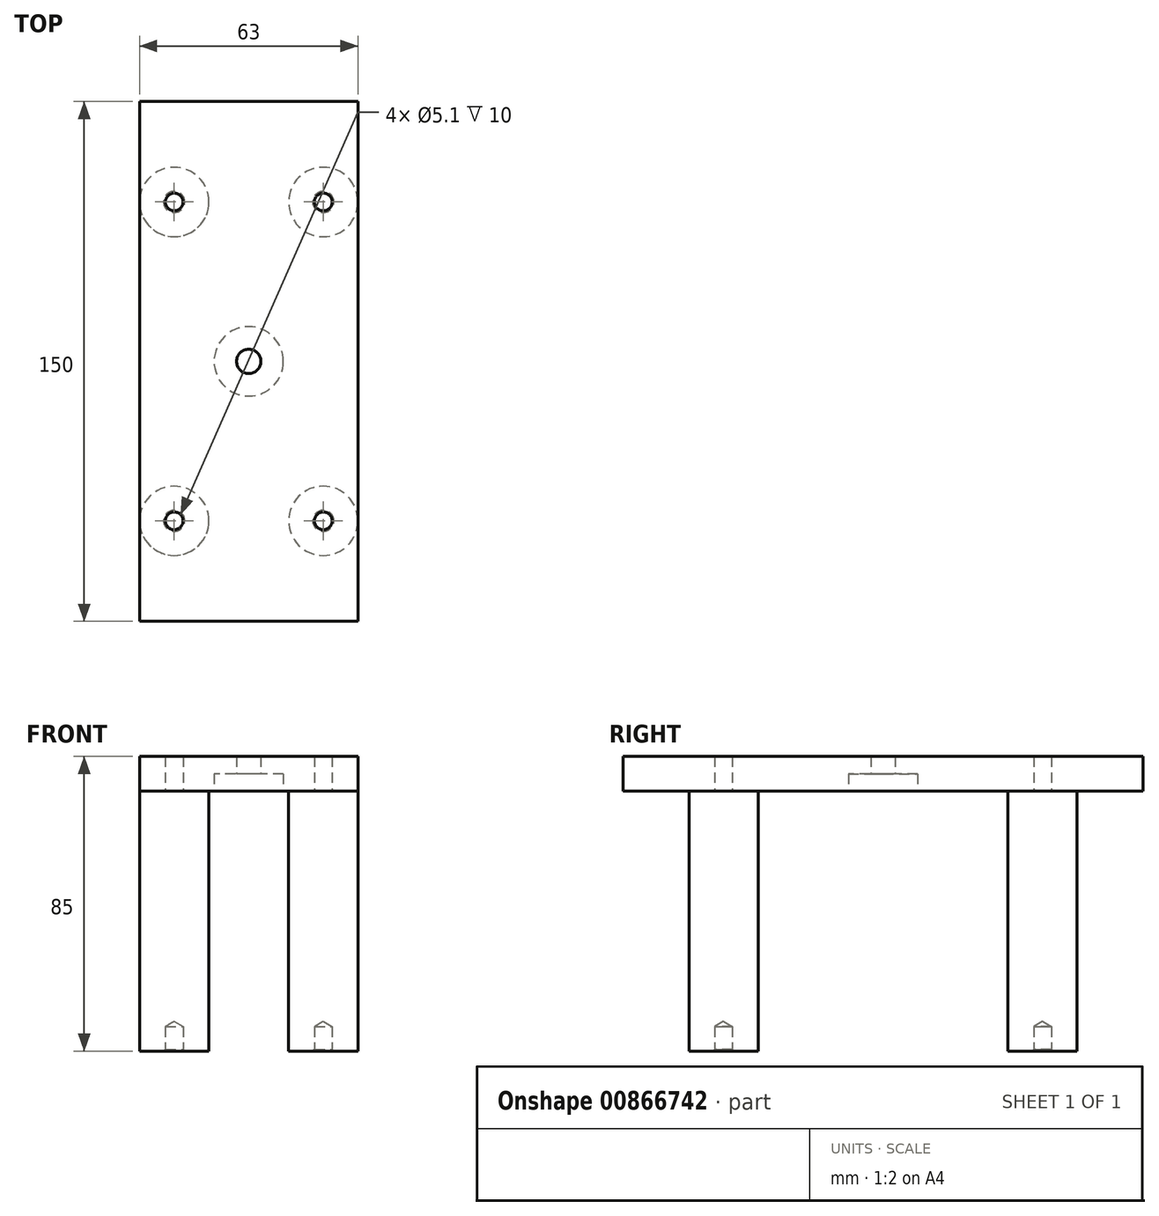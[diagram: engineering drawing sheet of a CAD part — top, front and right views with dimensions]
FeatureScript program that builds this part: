
annotation { "Feature Type Name" : "Feature", "Feature Type Description" : "" }
export const myFeature = defineFeature(function(context is Context, id is Id, definition is map)
    precondition{}
    {
        {
            assignVariable(context, id + "F0", {"variableType" : VariableType.LENGTH, "name" : "PillarLength", "lengthValue" : 75 * mm});
        }
        {
            assignVariable(context, id + "F1", {"variableType" : VariableType.LENGTH, "name" : "RackThickness", "lengthValue" : 10 * mm});
        }
        {
            assignVariable(context, id + "F2", {"variableType" : VariableType.LENGTH, "name" : "InsertWidth", "lengthValue" : 5.1 * mm});
        }
        {
            assignVariable(context, id + "F3", {"variableType" : VariableType.LENGTH, "name" : "InsertDepth", "lengthValue" : 6.4 * mm});
        }
        {
            var Q0;
            Q0=qCreatedBy(makeId("Top.planeOp"),FACE);
            var sketch = newSketch(context, id + "F4", { "sketchPlane" : qUnion([Q0])});
            skLineSegment(sketch, "E0.bottom", {"start": v(31.5, -75) * mm, "end": v(-31.5, -75) * mm});
            skLineSegment(sketch, "E0.top", {"start": v(31.5, 75) * mm, "end": v(-31.5, 75) * mm});
            skLineSegment(sketch, "E0.left", {"start": v(31.5, -75) * mm, "end": v(31.5, 75) * mm});
            skLineSegment(sketch, "E0.right", {"start": v(-31.5, -75) * mm, "end": v(-31.5, 75) * mm});
            skPoint(sketch, "E0.middle", {"position": v(0, 0) * mm});
            skLineSegment(sketch, "E1.bottom", {"start": v(21.5, 46) * mm, "end": v(-21.5, 46) * mm});
            skLineSegment(sketch, "E1.top", {"start": v(21.5, -46) * mm, "end": v(-21.5, -46) * mm});
            skLineSegment(sketch, "E1.left", {"start": v(21.5, 46) * mm, "end": v(21.5, -46) * mm});
            skLineSegment(sketch, "E1.right", {"start": v(-21.5, 46) * mm, "end": v(-21.5, -46) * mm});
            skCircle(sketch, "E2", {"center": v(-21.5, 46) * mm, "radius": 10 * mm});
            skCircle(sketch, "E3", {"center": v(21.5, 46) * mm, "radius": 10 * mm});
            skCircle(sketch, "E4", {"center": v(-21.5, -46) * mm, "radius": 10 * mm});
            skCircle(sketch, "E5", {"center": v(21.5, -46) * mm, "radius": 10 * mm});
            skCircle(sketch, "E6", {"center": v(-21.5, 46) * mm, "radius": 2.55 * mm});
            skCircle(sketch, "E7", {"center": v(21.5, 46) * mm, "radius": 2.55 * mm});
            skCircle(sketch, "E8", {"center": v(-21.5, -46) * mm, "radius": 2.55 * mm});
            skCircle(sketch, "E9", {"center": v(21.5, -46) * mm, "radius": 2.55 * mm});
            skSolve(sketch);
        }
        {
            var Q0;
            {var subQ0=sQuery(id+"F4.wireOp",EDGE,"E5");var subQ1=sQuery(id+"F4.wireOp",EDGE,"E0.left");var subQ2=makeQuery(id+"F4.imprint","INTERSECT",VERTEX,{"derivedFrom":[subQ1,subQ0]});Q0=makeQuery(id+"F4.imprint","IMPRINT",FACE,{"disambiguationData":[TD([[makeQuery(id+"F4.imprint","IMPRINT",EDGE,{"disambiguationData":[TD([[subQ2,-1.0]])],"derivedFrom":subQ1}),1.0]])]});}
            var Q1;
            {var subQ1=sQuery(id+"F4.wireOp",EDGE,"E0.bottom");Q1=makeQuery(id+"F4.imprint","IMPRINT",FACE,{"disambiguationData":[TD([[makeQuery(id+"F4.imprint","IMPRINT",EDGE,{"derivedFrom":subQ1}),-1.0]])]});}
            var Q2;
            {var subQ0=sQuery(id+"F4.wireOp",EDGE,"E4");var subQ1=sQuery(id+"F4.wireOp",EDGE,"E0.right");var subQ2=makeQuery(id+"F4.imprint","INTERSECT",VERTEX,{"derivedFrom":[subQ1,subQ0]});Q2=makeQuery(id+"F4.imprint","IMPRINT",FACE,{"disambiguationData":[TD([[makeQuery(id+"F4.imprint","IMPRINT",EDGE,{"disambiguationData":[TD([[subQ2,-1.0]])],"derivedFrom":subQ1}),-1.0]])]});}
            var Q3;
            {var subQ5=sQuery(id+"F4.wireOp",EDGE,"E3");var subQ13=sQuery(id+"F4.wireOp",EDGE,"E1.bottom");var subQ14=makeQuery(id+"F4.imprint","INTERSECT",VERTEX,{"derivedFrom":[subQ13,subQ5]});Q3=makeQuery(id+"F4.imprint","IMPRINT",FACE,{"disambiguationData":[TD([[makeQuery(id+"F4.imprint","IMPRINT",EDGE,{"disambiguationData":[TD([[subQ14,-1.0]])],"derivedFrom":subQ13}),1.0]])]});}
            var Q4;
            {var subQ0=sQuery(id+"F4.wireOp",EDGE,"E4");var subQ4=sQuery(id+"F4.wireOp",EDGE,"E1.top");var subQ5=makeQuery(id+"F4.imprint","INTERSECT",VERTEX,{"derivedFrom":[subQ4,subQ0]});Q4=makeQuery(id+"F4.imprint","IMPRINT",FACE,{"disambiguationData":[TD([[makeQuery(id+"F4.imprint","IMPRINT",EDGE,{"disambiguationData":[TD([[subQ5,-1.0]])],"derivedFrom":subQ4}),1.0]])]});}
            var Q5;
            {var subQ0=sQuery(id+"F4.wireOp",EDGE,"E4");var subQ1=sQuery(id+"F4.wireOp",EDGE,"E1.top");var subQ2=makeQuery(id+"F4.imprint","INTERSECT",VERTEX,{"derivedFrom":[subQ1,subQ0]});Q5=makeQuery(id+"F4.imprint","IMPRINT",FACE,{"disambiguationData":[TD([[makeQuery(id+"F4.imprint","IMPRINT",EDGE,{"disambiguationData":[TD([[subQ2,-1.0]])],"derivedFrom":subQ1}),-1.0]])]});}
            var Q6;
            {var subQ0=sQuery(id+"F4.wireOp",EDGE,"E1.right");var subQ1=sQuery(id+"F4.wireOp",EDGE,"E1.top");var subQ2=makeQuery(id+"F4.imprint","INTERSECT",VERTEX,{"derivedFrom":[subQ1,subQ0]});Q6=makeQuery(id+"F4.imprint","IMPRINT",FACE,{"disambiguationData":[TD([[makeQuery(id+"F4.imprint","IMPRINT",EDGE,{"disambiguationData":[TD([[subQ2,1.0]])],"derivedFrom":subQ1}),1.0]])]});}
            var Q7;
            {var subQ0=sQuery(id+"F4.wireOp",EDGE,"E1.right");var subQ1=sQuery(id+"F4.wireOp",EDGE,"E1.top");var subQ2=makeQuery(id+"F4.imprint","INTERSECT",VERTEX,{"derivedFrom":[subQ1,subQ0]});Q7=makeQuery(id+"F4.imprint","IMPRINT",FACE,{"disambiguationData":[TD([[makeQuery(id+"F4.imprint","IMPRINT",EDGE,{"disambiguationData":[TD([[subQ2,1.0]])],"derivedFrom":subQ1}),-1.0]])]});}
            var Q8;
            {var subQ4=sQuery(id+"F4.wireOp",EDGE,"E9");var subQ6=sQuery(id+"F4.wireOp",EDGE,"E1.top");var subQ8=makeQuery(id+"F4.imprint","INTERSECT",VERTEX,{"derivedFrom":[subQ6,subQ4]});Q8=makeQuery(id+"F4.imprint","IMPRINT",FACE,{"disambiguationData":[TD([[makeQuery(id+"F4.imprint","IMPRINT",EDGE,{"disambiguationData":[TD([[subQ8,-1.0]])],"derivedFrom":subQ6}),1.0]])]});}
            var Q9;
            {var subQ0=sQuery(id+"F4.wireOp",EDGE,"E1.left");var subQ1=sQuery(id+"F4.wireOp",EDGE,"E1.top");var subQ2=makeQuery(id+"F4.imprint","INTERSECT",VERTEX,{"derivedFrom":[subQ1,subQ0]});Q9=makeQuery(id+"F4.imprint","IMPRINT",FACE,{"disambiguationData":[TD([[makeQuery(id+"F4.imprint","IMPRINT",EDGE,{"disambiguationData":[TD([[subQ2,-1.0]])],"derivedFrom":subQ1}),-1.0]])]});}
            var Q10;
            {var subQ0=sQuery(id+"F4.wireOp",EDGE,"E1.left");var subQ1=sQuery(id+"F4.wireOp",EDGE,"E1.top");var subQ2=makeQuery(id+"F4.imprint","INTERSECT",VERTEX,{"derivedFrom":[subQ1,subQ0]});Q10=makeQuery(id+"F4.imprint","IMPRINT",FACE,{"disambiguationData":[TD([[makeQuery(id+"F4.imprint","IMPRINT",EDGE,{"disambiguationData":[TD([[subQ2,-1.0]])],"derivedFrom":subQ1}),1.0]])]});}
            var Q11;
            {var subQ0=sQuery(id+"F4.wireOp",EDGE,"E9");var subQ1=sQuery(id+"F4.wireOp",EDGE,"E1.top");var subQ2=makeQuery(id+"F4.imprint","INTERSECT",VERTEX,{"derivedFrom":[subQ1,subQ0]});Q11=makeQuery(id+"F4.imprint","IMPRINT",FACE,{"disambiguationData":[TD([[makeQuery(id+"F4.imprint","IMPRINT",EDGE,{"disambiguationData":[TD([[subQ2,-1.0]])],"derivedFrom":subQ1}),-1.0]])]});}
            var Q12;
            {var subQ0=sQuery(id+"F4.wireOp",EDGE,"E7");var subQ1=sQuery(id+"F4.wireOp",EDGE,"E1.bottom");var subQ2=makeQuery(id+"F4.imprint","INTERSECT",VERTEX,{"derivedFrom":[subQ1,subQ0]});Q12=makeQuery(id+"F4.imprint","IMPRINT",FACE,{"disambiguationData":[TD([[makeQuery(id+"F4.imprint","IMPRINT",EDGE,{"disambiguationData":[TD([[subQ2,-1.0]])],"derivedFrom":subQ1}),1.0]])]});}
            var Q13;
            {var subQ0=sQuery(id+"F4.wireOp",EDGE,"E1.left");var subQ1=sQuery(id+"F4.wireOp",EDGE,"E1.bottom");var subQ2=makeQuery(id+"F4.imprint","INTERSECT",VERTEX,{"derivedFrom":[subQ1,subQ0]});Q13=makeQuery(id+"F4.imprint","IMPRINT",FACE,{"disambiguationData":[TD([[makeQuery(id+"F4.imprint","IMPRINT",EDGE,{"disambiguationData":[TD([[subQ2,-1.0]])],"derivedFrom":subQ1}),1.0]])]});}
            var Q14;
            {var subQ0=sQuery(id+"F4.wireOp",EDGE,"E1.left");var subQ1=sQuery(id+"F4.wireOp",EDGE,"E1.bottom");var subQ2=makeQuery(id+"F4.imprint","INTERSECT",VERTEX,{"derivedFrom":[subQ1,subQ0]});Q14=makeQuery(id+"F4.imprint","IMPRINT",FACE,{"disambiguationData":[TD([[makeQuery(id+"F4.imprint","IMPRINT",EDGE,{"disambiguationData":[TD([[subQ2,-1.0]])],"derivedFrom":subQ1}),-1.0]])]});}
            var Q15;
            {var subQ4=sQuery(id+"F4.wireOp",EDGE,"E1.bottom");var subQ6=sQuery(id+"F4.wireOp",EDGE,"E7");var subQ7=makeQuery(id+"F4.imprint","INTERSECT",VERTEX,{"derivedFrom":[subQ4,subQ6]});Q15=makeQuery(id+"F4.imprint","IMPRINT",FACE,{"disambiguationData":[TD([[makeQuery(id+"F4.imprint","IMPRINT",EDGE,{"disambiguationData":[TD([[subQ7,-1.0]])],"derivedFrom":subQ4}),-1.0]])]});}
            var Q16;
            {var subQ0=sQuery(id+"F4.wireOp",EDGE,"E2");var subQ1=sQuery(id+"F4.wireOp",EDGE,"E1.bottom");var subQ2=makeQuery(id+"F4.imprint","INTERSECT",VERTEX,{"derivedFrom":[subQ1,subQ0]});Q16=makeQuery(id+"F4.imprint","IMPRINT",FACE,{"disambiguationData":[TD([[makeQuery(id+"F4.imprint","IMPRINT",EDGE,{"disambiguationData":[TD([[subQ2,-1.0]])],"derivedFrom":subQ1}),1.0]])]});}
            var Q17;
            {var subQ0=sQuery(id+"F4.wireOp",EDGE,"E1.right");var subQ1=sQuery(id+"F4.wireOp",EDGE,"E1.bottom");var subQ2=makeQuery(id+"F4.imprint","INTERSECT",VERTEX,{"derivedFrom":[subQ1,subQ0]});Q17=makeQuery(id+"F4.imprint","IMPRINT",FACE,{"disambiguationData":[TD([[makeQuery(id+"F4.imprint","IMPRINT",EDGE,{"disambiguationData":[TD([[subQ2,1.0]])],"derivedFrom":subQ1}),1.0]])]});}
            var Q18;
            {var subQ0=sQuery(id+"F4.wireOp",EDGE,"E1.right");var subQ1=sQuery(id+"F4.wireOp",EDGE,"E1.bottom");var subQ2=makeQuery(id+"F4.imprint","INTERSECT",VERTEX,{"derivedFrom":[subQ1,subQ0]});Q18=makeQuery(id+"F4.imprint","IMPRINT",FACE,{"disambiguationData":[TD([[makeQuery(id+"F4.imprint","IMPRINT",EDGE,{"disambiguationData":[TD([[subQ2,1.0]])],"derivedFrom":subQ1}),-1.0]])]});}
            var Q19;
            {var subQ0=sQuery(id+"F4.wireOp",EDGE,"E2");var subQ2=sQuery(id+"F4.wireOp",EDGE,"E1.bottom");var subQ3=makeQuery(id+"F4.imprint","INTERSECT",VERTEX,{"derivedFrom":[subQ2,subQ0]});Q19=makeQuery(id+"F4.imprint","IMPRINT",FACE,{"disambiguationData":[TD([[makeQuery(id+"F4.imprint","IMPRINT",EDGE,{"disambiguationData":[TD([[subQ3,-1.0]])],"derivedFrom":subQ2}),-1.0]])]});}
            var Q20;
            {var subQ6=sQuery(id+"F4.wireOp",EDGE,"E0.top");Q20=makeQuery(id+"F4.imprint","IMPRINT",FACE,{"disambiguationData":[TD([[makeQuery(id+"F4.imprint","IMPRINT",EDGE,{"derivedFrom":subQ6}),1.0]])]});}
            extrude(context, id + "F5", {"entities" : qUnion([Q0, Q1, Q2, Q3, Q4, Q5, Q6, Q7, Q8, Q9, Q10, Q11, Q12, Q13, Q14, Q15, Q16, Q17, Q18, Q19, Q20]), "depth" : getVariable(context, 'RackThickness'), "offsetDistance" : 25 * mm});
        }
        {
            var Q0;
            {var subQ0=sQuery(id+"F4.wireOp",EDGE,"E7");var subQ1=sQuery(id+"F4.wireOp",EDGE,"E1.bottom");var subQ2=makeQuery(id+"F4.imprint","INTERSECT",VERTEX,{"derivedFrom":[subQ1,subQ0]});Q0=makeQuery(id+"F4.imprint","IMPRINT",FACE,{"disambiguationData":[TD([[makeQuery(id+"F4.imprint","IMPRINT",EDGE,{"disambiguationData":[TD([[subQ2,-1.0]])],"derivedFrom":subQ1}),1.0]])]});}
            var Q1;
            {var subQ4=sQuery(id+"F4.wireOp",EDGE,"E1.bottom");var subQ6=sQuery(id+"F4.wireOp",EDGE,"E7");var subQ7=makeQuery(id+"F4.imprint","INTERSECT",VERTEX,{"derivedFrom":[subQ4,subQ6]});Q1=makeQuery(id+"F4.imprint","IMPRINT",FACE,{"disambiguationData":[TD([[makeQuery(id+"F4.imprint","IMPRINT",EDGE,{"disambiguationData":[TD([[subQ7,-1.0]])],"derivedFrom":subQ4}),-1.0]])]});}
            var Q2;
            {var subQ0=sQuery(id+"F4.wireOp",EDGE,"E1.left");var subQ1=sQuery(id+"F4.wireOp",EDGE,"E1.bottom");var subQ2=makeQuery(id+"F4.imprint","INTERSECT",VERTEX,{"derivedFrom":[subQ1,subQ0]});Q2=makeQuery(id+"F4.imprint","IMPRINT",FACE,{"disambiguationData":[TD([[makeQuery(id+"F4.imprint","IMPRINT",EDGE,{"disambiguationData":[TD([[subQ2,-1.0]])],"derivedFrom":subQ1}),-1.0]])]});}
            var Q3;
            {var subQ0=sQuery(id+"F4.wireOp",EDGE,"E1.left");var subQ1=sQuery(id+"F4.wireOp",EDGE,"E1.bottom");var subQ2=makeQuery(id+"F4.imprint","INTERSECT",VERTEX,{"derivedFrom":[subQ1,subQ0]});Q3=makeQuery(id+"F4.imprint","IMPRINT",FACE,{"disambiguationData":[TD([[makeQuery(id+"F4.imprint","IMPRINT",EDGE,{"disambiguationData":[TD([[subQ2,-1.0]])],"derivedFrom":subQ1}),1.0]])]});}
            var Q4;
            {var subQ0=sQuery(id+"F4.wireOp",EDGE,"E2");var subQ1=sQuery(id+"F4.wireOp",EDGE,"E1.bottom");var subQ2=makeQuery(id+"F4.imprint","INTERSECT",VERTEX,{"derivedFrom":[subQ1,subQ0]});Q4=makeQuery(id+"F4.imprint","IMPRINT",FACE,{"disambiguationData":[TD([[makeQuery(id+"F4.imprint","IMPRINT",EDGE,{"disambiguationData":[TD([[subQ2,-1.0]])],"derivedFrom":subQ1}),1.0]])]});}
            var Q5;
            {var subQ0=sQuery(id+"F4.wireOp",EDGE,"E2");var subQ2=sQuery(id+"F4.wireOp",EDGE,"E1.bottom");var subQ3=makeQuery(id+"F4.imprint","INTERSECT",VERTEX,{"derivedFrom":[subQ2,subQ0]});Q5=makeQuery(id+"F4.imprint","IMPRINT",FACE,{"disambiguationData":[TD([[makeQuery(id+"F4.imprint","IMPRINT",EDGE,{"disambiguationData":[TD([[subQ3,-1.0]])],"derivedFrom":subQ2}),-1.0]])]});}
            var Q6;
            {var subQ0=sQuery(id+"F4.wireOp",EDGE,"E1.right");var subQ1=sQuery(id+"F4.wireOp",EDGE,"E1.bottom");var subQ2=makeQuery(id+"F4.imprint","INTERSECT",VERTEX,{"derivedFrom":[subQ1,subQ0]});Q6=makeQuery(id+"F4.imprint","IMPRINT",FACE,{"disambiguationData":[TD([[makeQuery(id+"F4.imprint","IMPRINT",EDGE,{"disambiguationData":[TD([[subQ2,1.0]])],"derivedFrom":subQ1}),1.0]])]});}
            var Q7;
            {var subQ0=sQuery(id+"F4.wireOp",EDGE,"E1.right");var subQ1=sQuery(id+"F4.wireOp",EDGE,"E1.bottom");var subQ2=makeQuery(id+"F4.imprint","INTERSECT",VERTEX,{"derivedFrom":[subQ1,subQ0]});Q7=makeQuery(id+"F4.imprint","IMPRINT",FACE,{"disambiguationData":[TD([[makeQuery(id+"F4.imprint","IMPRINT",EDGE,{"disambiguationData":[TD([[subQ2,1.0]])],"derivedFrom":subQ1}),-1.0]])]});}
            var Q8;
            {var subQ0=sQuery(id+"F4.wireOp",EDGE,"E1.right");var subQ1=sQuery(id+"F4.wireOp",EDGE,"E1.top");var subQ2=makeQuery(id+"F4.imprint","INTERSECT",VERTEX,{"derivedFrom":[subQ1,subQ0]});Q8=makeQuery(id+"F4.imprint","IMPRINT",FACE,{"disambiguationData":[TD([[makeQuery(id+"F4.imprint","IMPRINT",EDGE,{"disambiguationData":[TD([[subQ2,1.0]])],"derivedFrom":subQ1}),1.0]])]});}
            var Q9;
            {var subQ0=sQuery(id+"F4.wireOp",EDGE,"E1.right");var subQ1=sQuery(id+"F4.wireOp",EDGE,"E1.top");var subQ2=makeQuery(id+"F4.imprint","INTERSECT",VERTEX,{"derivedFrom":[subQ1,subQ0]});Q9=makeQuery(id+"F4.imprint","IMPRINT",FACE,{"disambiguationData":[TD([[makeQuery(id+"F4.imprint","IMPRINT",EDGE,{"disambiguationData":[TD([[subQ2,1.0]])],"derivedFrom":subQ1}),-1.0]])]});}
            var Q10;
            {var subQ0=sQuery(id+"F4.wireOp",EDGE,"E4");var subQ1=sQuery(id+"F4.wireOp",EDGE,"E1.top");var subQ2=makeQuery(id+"F4.imprint","INTERSECT",VERTEX,{"derivedFrom":[subQ1,subQ0]});Q10=makeQuery(id+"F4.imprint","IMPRINT",FACE,{"disambiguationData":[TD([[makeQuery(id+"F4.imprint","IMPRINT",EDGE,{"disambiguationData":[TD([[subQ2,-1.0]])],"derivedFrom":subQ1}),-1.0]])]});}
            var Q11;
            {var subQ0=sQuery(id+"F4.wireOp",EDGE,"E4");var subQ4=sQuery(id+"F4.wireOp",EDGE,"E1.top");var subQ5=makeQuery(id+"F4.imprint","INTERSECT",VERTEX,{"derivedFrom":[subQ4,subQ0]});Q11=makeQuery(id+"F4.imprint","IMPRINT",FACE,{"disambiguationData":[TD([[makeQuery(id+"F4.imprint","IMPRINT",EDGE,{"disambiguationData":[TD([[subQ5,-1.0]])],"derivedFrom":subQ4}),1.0]])]});}
            var Q12;
            {var subQ0=sQuery(id+"F4.wireOp",EDGE,"E1.left");var subQ1=sQuery(id+"F4.wireOp",EDGE,"E1.top");var subQ2=makeQuery(id+"F4.imprint","INTERSECT",VERTEX,{"derivedFrom":[subQ1,subQ0]});Q12=makeQuery(id+"F4.imprint","IMPRINT",FACE,{"disambiguationData":[TD([[makeQuery(id+"F4.imprint","IMPRINT",EDGE,{"disambiguationData":[TD([[subQ2,-1.0]])],"derivedFrom":subQ1}),1.0]])]});}
            var Q13;
            {var subQ0=sQuery(id+"F4.wireOp",EDGE,"E1.left");var subQ1=sQuery(id+"F4.wireOp",EDGE,"E1.top");var subQ2=makeQuery(id+"F4.imprint","INTERSECT",VERTEX,{"derivedFrom":[subQ1,subQ0]});Q13=makeQuery(id+"F4.imprint","IMPRINT",FACE,{"disambiguationData":[TD([[makeQuery(id+"F4.imprint","IMPRINT",EDGE,{"disambiguationData":[TD([[subQ2,-1.0]])],"derivedFrom":subQ1}),-1.0]])]});}
            var Q14;
            {var subQ0=sQuery(id+"F4.wireOp",EDGE,"E9");var subQ1=sQuery(id+"F4.wireOp",EDGE,"E1.top");var subQ2=makeQuery(id+"F4.imprint","INTERSECT",VERTEX,{"derivedFrom":[subQ1,subQ0]});Q14=makeQuery(id+"F4.imprint","IMPRINT",FACE,{"disambiguationData":[TD([[makeQuery(id+"F4.imprint","IMPRINT",EDGE,{"disambiguationData":[TD([[subQ2,-1.0]])],"derivedFrom":subQ1}),-1.0]])]});}
            var Q15;
            {var subQ4=sQuery(id+"F4.wireOp",EDGE,"E9");var subQ6=sQuery(id+"F4.wireOp",EDGE,"E1.top");var subQ8=makeQuery(id+"F4.imprint","INTERSECT",VERTEX,{"derivedFrom":[subQ6,subQ4]});Q15=makeQuery(id+"F4.imprint","IMPRINT",FACE,{"disambiguationData":[TD([[makeQuery(id+"F4.imprint","IMPRINT",EDGE,{"disambiguationData":[TD([[subQ8,-1.0]])],"derivedFrom":subQ6}),1.0]])]});}
            extrude(context, id + "F6", {"entities" : qUnion([Q0, Q1, Q2, Q3, Q4, Q5, Q6, Q7, Q8, Q9, Q10, Q11, Q12, Q13, Q14, Q15]), "operationType" : NewBodyOperationType.ADD, "oppositeDirection" : true, "depth" : getVariable(context, 'PillarLength'), "offsetDistance" : 25 * mm});
        }
        {
            var Q0;
            Q0=makeQuery(id+"F6.opExtrude","CAP_FACE",FACE,{"disambiguationData":[OSD([sQuery(id+"F4.wireOp",EDGE,"E2")])],"isStart":false});
            var sketch = newSketch(context, id + "F7", { "sketchPlane" : qUnion([Q0])});
            skCircle(sketch, "E10", {"center": v(-21.5, -46) * mm, "radius": 2.55 * mm});
            skSolve(sketch);
        }
        {
            var Q0;
            Q0=makeQuery(id+"F6.opExtrude","CAP_FACE",FACE,{"disambiguationData":[OSD([sQuery(id+"F4.wireOp",EDGE,"E3")])],"isStart":false});
            var sketch = newSketch(context, id + "F8", { "sketchPlane" : qUnion([Q0])});
            skCircle(sketch, "E11", {"center": v(21.5, -46) * mm, "radius": 2.55 * mm});
            skSolve(sketch);
        }
        {
            var Q0;
            Q0=makeQuery(id+"F6.opExtrude","CAP_FACE",FACE,{"disambiguationData":[OSD([sQuery(id+"F4.wireOp",EDGE,"E4")])],"isStart":false});
            var sketch = newSketch(context, id + "F9", { "sketchPlane" : qUnion([Q0])});
            skCircle(sketch, "E12", {"center": v(-21.5, 46) * mm, "radius": 2.55 * mm});
            skSolve(sketch);
        }
        {
            var Q0;
            Q0=makeQuery(id+"F6.opExtrude","CAP_FACE",FACE,{"disambiguationData":[OSD([sQuery(id+"F4.wireOp",EDGE,"E5")])],"isStart":false});
            var sketch = newSketch(context, id + "F10", { "sketchPlane" : qUnion([Q0])});
            skCircle(sketch, "E13", {"center": v(21.5, 46) * mm, "radius": 2.55 * mm});
            skSolve(sketch);
        }
        {
            var Q0;
            Q0=sQuery(id+"F7.wireOp",VERTEX,"E10.center");
            var Q1;
            Q1=sQuery(id+"F9.wireOp",VERTEX,"E12.center");
            var Q2;
            Q2=sQuery(id+"F10.wireOp",VERTEX,"E13.center");
            var Q3;
            Q3=sQuery(id+"F8.wireOp",VERTEX,"E11.center");
            var Q4;
            Q4=makeQuery(id+"F5.opExtrude","SWEPT_BODY",BODY,{"disambiguationData":[OSD([sQuery(id+"F4.wireOp",EDGE,"E0.bottom"),sQuery(id+"F4.wireOp",EDGE,"E0.top"),sQuery(id+"F4.wireOp",EDGE,"E0.left"),sQuery(id+"F4.wireOp",EDGE,"E0.right")])]});
            hole(context, id + "F11", {"style" : HoleStyle.C_SINK, "endStyle" : HoleEndStyle.BLIND, "holeDiameter" : getVariable(context, 'InsertWidth'), "cSinkDiameter" : (getVariable(context, 'InsertWidth') * 1.2), "cSinkAngle" : 90 * degree, "majorDiameter" : 5 * mm, "holeDepth" : (getVariable(context, 'InsertDepth') * 1.1), "isTappedThrough" : true, "tappedDepth" : 12 * mm, "tapClearance" : 3, "startFromSketch" : true, "locations" : qUnion([Q0, Q1, Q2, Q3]), "scope" : qUnion([Q4])});
        }
        {
            var Q0;
            Q0=sQuery(id+"F4.wireOp",VERTEX,"E1.bottom.end");
            var Q1;
            Q1=sQuery(id+"F4.wireOp",VERTEX,"E1.bottom.start");
            var Q2;
            Q2=sQuery(id+"F4.wireOp",VERTEX,"E1.top.end");
            var Q3;
            Q3=sQuery(id+"F4.wireOp",VERTEX,"E1.top.start");
            var Q4;
            Q4=makeQuery(id+"F5.opExtrude","SWEPT_BODY",BODY,{"disambiguationData":[OSD([sQuery(id+"F4.wireOp",EDGE,"E0.bottom"),sQuery(id+"F4.wireOp",EDGE,"E0.top"),sQuery(id+"F4.wireOp",EDGE,"E0.left"),sQuery(id+"F4.wireOp",EDGE,"E0.right")])]});
            hole(context, id + "F12", {"style" : HoleStyle.SIMPLE, "endStyle" : HoleEndStyle.BLIND, "oppositeDirection" : true, "holeDiameter" : getVariable(context, 'InsertWidth'), "majorDiameter" : 5 * mm, "holeDepth" : (getVariable(context, 'RackThickness') * 1.1), "isTappedThrough" : true, "tappedDepth" : 12 * mm, "tapClearance" : 3, "startFromSketch" : true, "locations" : qUnion([Q0, Q1, Q2, Q3]), "scope" : qUnion([Q4])});
        }
        {
            var Q0;
            {var subQ5=sQuery(id+"F4.wireOp",EDGE,"E3");var subQ13=sQuery(id+"F4.wireOp",EDGE,"E1.bottom");var subQ14=makeQuery(id+"F4.imprint","INTERSECT",VERTEX,{"derivedFrom":[subQ13,subQ5]});Q0=makeQuery(id+"F4.imprint","IMPRINT",FACE,{"disambiguationData":[TD([[makeQuery(id+"F4.imprint","IMPRINT",EDGE,{"disambiguationData":[TD([[subQ14,-1.0]])],"derivedFrom":subQ13}),1.0]])]});}
            var sketch = newSketch(context, id + "F13", { "sketchPlane" : qUnion([Q0])});
            skCircle(sketch, "E14", {"center": v(0, 0) * mm, "radius": 3.5 * mm});
            skSolve(sketch);
        }
        {
            var Q0;
            Q0=makeQuery(id+"F13.imprint","IMPRINT",FACE,{"disambiguationData":[TD([[makeQuery(id+"F13.imprint","IMPRINT",EDGE,{"derivedFrom":sQuery(id+"F13.wireOp",EDGE,"E14")}),1.0]])]});
            extrude(context, id + "F14", {"entities" : qUnion([Q0]), "operationType" : NewBodyOperationType.REMOVE, "depth" : 25 * mm, "offsetDistance" : 25 * mm});
        }
        {
            var Q0;
            {var subQ5=sQuery(id+"F4.wireOp",EDGE,"E3");var subQ13=sQuery(id+"F4.wireOp",EDGE,"E1.bottom");var subQ14=makeQuery(id+"F4.imprint","INTERSECT",VERTEX,{"derivedFrom":[subQ13,subQ5]});Q0=makeQuery(id+"F4.imprint","IMPRINT",FACE,{"disambiguationData":[TD([[makeQuery(id+"F4.imprint","IMPRINT",EDGE,{"disambiguationData":[TD([[subQ14,-1.0]])],"derivedFrom":subQ13}),1.0]])]});}
            var sketch = newSketch(context, id + "F15", { "sketchPlane" : qUnion([Q0])});
            skCircle(sketch, "E15", {"center": v(0, 0) * mm, "radius": 10 * mm});
            skSolve(sketch);
        }
        {
            var Q0;
            Q0=makeQuery(id+"F15.imprint","IMPRINT",FACE,{"disambiguationData":[TD([[makeQuery(id+"F15.imprint","IMPRINT",EDGE,{"derivedFrom":sQuery(id+"F15.wireOp",EDGE,"E15")}),1.0]])]});
            extrude(context, id + "F16", {"entities" : qUnion([Q0]), "operationType" : NewBodyOperationType.REMOVE, "depth" : .5 * getVariable(context, 'RackThickness'), "offsetDistance" : 25 * mm});
        }
    });
